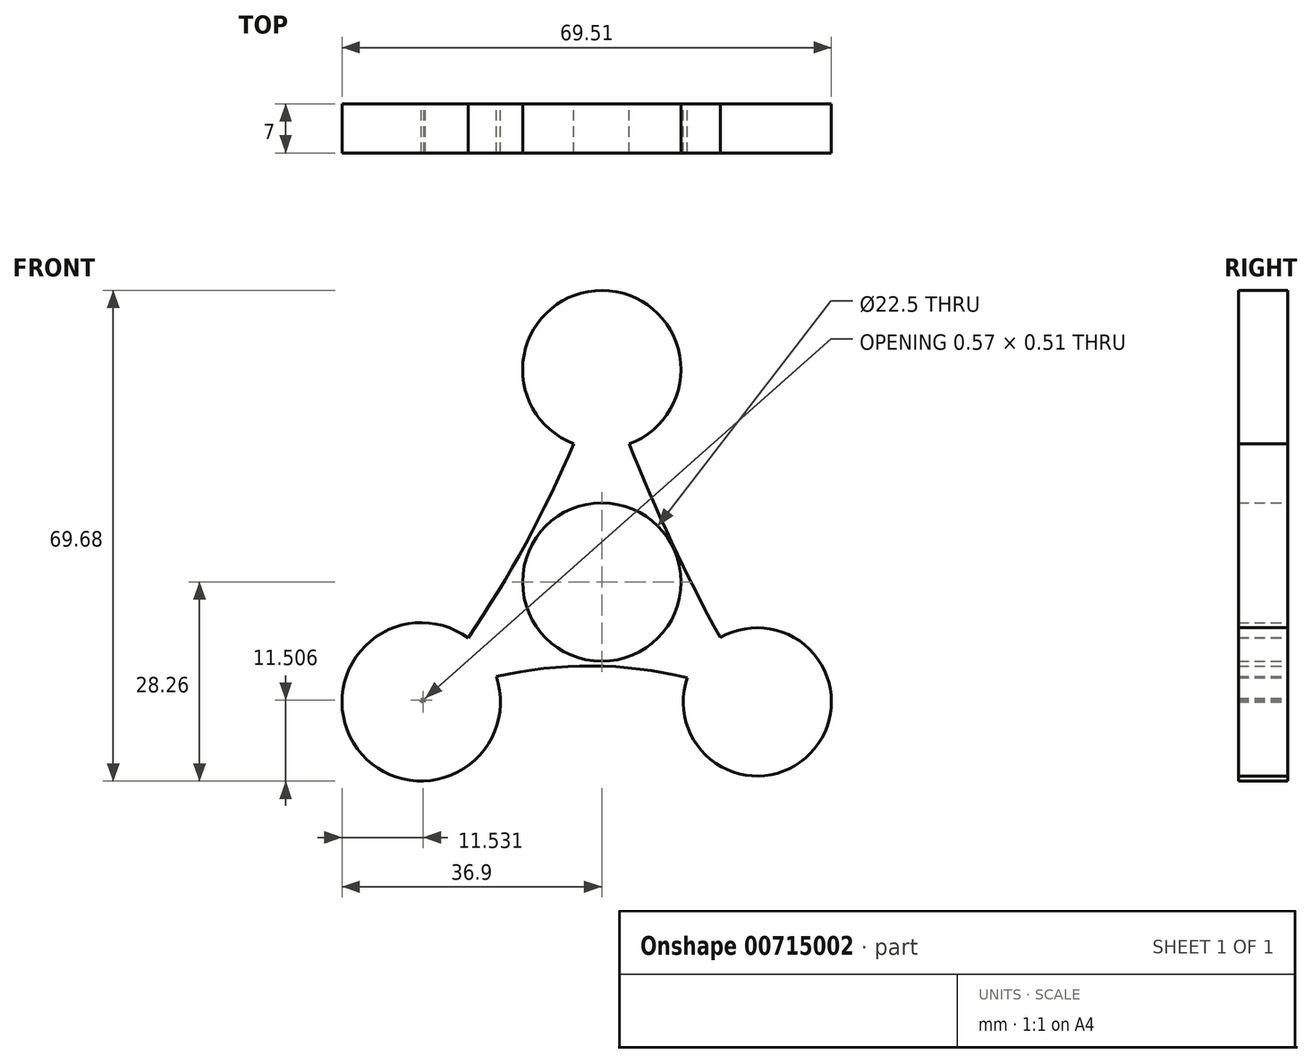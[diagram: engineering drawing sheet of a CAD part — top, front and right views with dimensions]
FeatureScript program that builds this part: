
annotation { "Feature Type Name" : "Feature", "Feature Type Description" : "" }
export const myFeature = defineFeature(function(context is Context, id is Id, definition is map)
    precondition{}
    {
        {
            var Q0;
            Q0=qCreatedBy(makeId("Front.planeOp"),FACE);
            var sketch = newSketch(context, id + "F0", { "sketchPlane" : qUnion([Q0])});
            skCircle(sketch, "E0", {"center": v(0, 0) * mm, "radius": 11.25 * mm});
            skCircle(sketch, "E1", {"center": v(-25.65, -17) * mm, "radius": 11.25 * mm});
            skCircle(sketch, "E2", {"center": v(22.08, -17) * mm, "radius": 10.53 * mm});
            skCircle(sketch, "E3", {"center": v(0, 30.17) * mm, "radius": 11.25 * mm});
            skLineSegment(sketch, "E4", {"start": v(0, 30.17) * mm, "end": v(0, 0) * mm});
            skLineSegment(sketch, "E5", {"start": v(0, 0) * mm, "end": v(22.08, -17) * mm});
            skLineSegment(sketch, "E6", {"start": v(0, 0) * mm, "end": v(-25.65, -17) * mm});
            skArc(sketch, "E7", {"start": v(-25.65, -17) * mm, "mid": v(-10.8, 5.48) * mm, "end": v(0, 30.17) * mm});
            skArc(sketch, "E8", {"start": v(0, 30.17) * mm, "mid": v(9.78, 5.99) * mm, "end": v(22.08, -17) * mm});
            skArc(sketch, "E9", {"start": v(22.08, -17) * mm, "mid": v(-1.79, -11.9) * mm, "end": v(-25.65, -17) * mm});
            skArc(sketch, "E10.trimOffspring", {"start": v(-25.25, -16.5) * mm, "mid": v(-25.17, -16.63) * mm, "end": v(-25.08, -16.76) * mm});
            skSolve(sketch);
        }
        {
            var Q0;
            Q0 = qSketchRegion(id + "F0", true);
            extrude(context, id + "F1", {"entities" : qUnion([Q0]), "depth" : 7 * mm, "offsetDistance" : 25 * mm});
        }
    });
